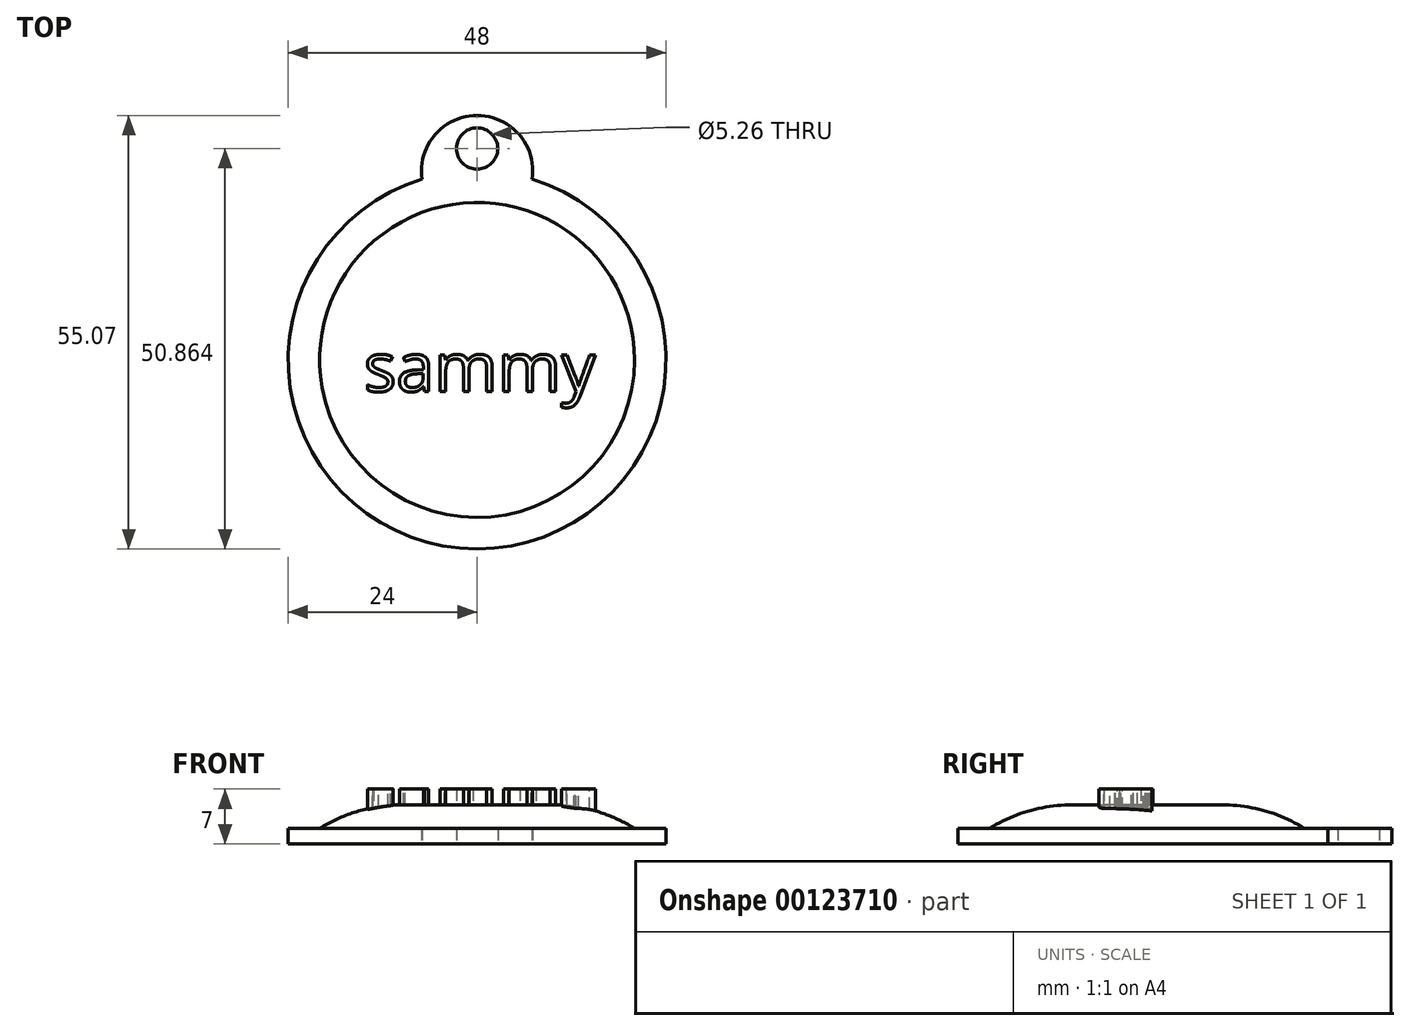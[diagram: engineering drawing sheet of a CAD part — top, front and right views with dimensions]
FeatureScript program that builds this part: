
annotation { "Feature Type Name" : "Feature", "Feature Type Description" : "" }
export const myFeature = defineFeature(function(context is Context, id is Id, definition is map)
    precondition{}
    {
        {
            var Q0;
            Q0=qCreatedBy(makeId("Top.planeOp"),FACE);
            var sketch = newSketch(context, id + "F0", { "sketchPlane" : qUnion([Q0])});
            skCircle(sketch, "E0", {"center": v(0, 0) * mm, "radius": 20 * mm});
            skCircle(sketch, "E1.0", {"center": v(0, 0) * mm, "radius": 24 * mm});
            skSolve(sketch);
        }
        {
            var Q0;
            Q0=makeQuery(id+"F0.imprint","IMPRINT",FACE,{"disambiguationData":[TD([[makeQuery(id+"F0.imprint","IMPRINT",EDGE,{"derivedFrom":sQuery(id+"F0.wireOp",EDGE,"E0")}),1.0]])]});
            var sketch = newSketch(context, id + "F1", { "sketchPlane" : qUnion([Q0])});
            skCircle(sketch, "E2", {"center": v(0, 0) * mm, "radius": 20 * mm});
            skSolve(sketch);
        }
        {
            var Q0;
            Q0 = qSketchRegion(id + "F1", true);
            extrude(context, id + "F2", {"entities" : qUnion([Q0]), "depth" : 5 * mm});
        }
        {
            var Q0;
            Q0=makeQuery(id+"F2.opExtrude","CAP_FACE",FACE,{"disambiguationData":[OSD([sQuery(id+"F1.wireOp",EDGE,"E2")])],"isStart":false});
            var sketch = newSketch(context, id + "F3", { "sketchPlane" : qUnion([Q0])});
            skText(sketch, "E3", { "text": "sammy", "fontName": "OpenSans-Regular.ttf"});
            const initialGuessF3  = {"E3": [-0.01439, -0.004, 1, 0, 0.00624]};
            skSetInitialGuess(sketch, initialGuessF3);
            skSolve(sketch);
        }
        {
            var Q0;
            Q0 = qSketchRegion(id + "F3", true);
            extrude(context, id + "F4", {"entities" : qUnion([Q0]), "operationType" : NewBodyOperationType.ADD, "endBound" : BoundingType.SYMMETRIC, "oppositeDirection" : true, "depth" : 4 * mm});
        }
        {
            var Q0;
            Q0=makeQuery(id+"F0.imprint","IMPRINT",FACE,{"disambiguationData":[TD([[makeQuery(id+"F0.imprint","IMPRINT",EDGE,{"derivedFrom":sQuery(id+"F0.wireOp",EDGE,"E0")}),-1.0]])]});
            extrude(context, id + "F5", {"entities" : qUnion([Q0]), "operationType" : NewBodyOperationType.ADD, "depth" : 2 * mm});
        }
        {
            var Q0;
            Q0=makeQuery(id+"F5.opExtrude","CAP_FACE",FACE,{"disambiguationData":[OSD([sQuery(id+"F0.wireOp",EDGE,"E0"),sQuery(id+"F0.wireOp",EDGE,"E1.0")])],"isStart":true});
            var sketch = newSketch(context, id + "F6", { "sketchPlane" : qUnion([Q0])});
            skCircle(sketch, "E4.0", {"center": v(0, 0) * mm, "radius": 20 * mm});
            skCircle(sketch, "E4.1", {"center": v(0, 0) * mm, "radius": 24 * mm});
            skArc(sketch, "E5", {"start": v(-7, -22.96) * mm, "mid": v(0, -31.07) * mm, "end": v(7, -22.96) * mm});
            skSolve(sketch);
        }
        {
            var Q0;
            {var subQ0=sQuery(id+"F6.wireOp",EDGE,"E5");Q0=makeQuery(id+"F6.imprint","IMPRINT",FACE,{"disambiguationData":[TD([[makeQuery(id+"F6.imprint","IMPRINT",EDGE,{"derivedFrom":subQ0}),1.0]])]});}
            extrude(context, id + "F7", {"entities" : qUnion([Q0]), "operationType" : NewBodyOperationType.ADD, "oppositeDirection" : true, "depth" : 2 * mm});
        }
        {
            var Q0;
            Q0=makeQuery(id+"F7.opExtrude","CAP_FACE",FACE,{"disambiguationData":[OSD([sQuery(id+"F6.wireOp",EDGE,"E4.1"),sQuery(id+"F6.wireOp",EDGE,"E5")])],"isStart":true});
            var sketch = newSketch(context, id + "F8", { "sketchPlane" : qUnion([Q0])});
            skCircle(sketch, "E6", {"center": v(0, -26.86) * mm, "radius": 2.63 * mm});
            skSolve(sketch);
        }
        {
            var Q0;
            Q0=makeQuery(id+"F8.imprint","IMPRINT",FACE,{"disambiguationData":[TD([[makeQuery(id+"F8.imprint","IMPRINT",EDGE,{"derivedFrom":sQuery(id+"F8.wireOp",EDGE,"E6")}),1.0]])]});
            extrude(context, id + "F9", {"entities" : qUnion([Q0]), "operationType" : NewBodyOperationType.REMOVE, "oppositeDirection" : true, "depth" : 2 * mm});
        }
        {
            var Q0;
            Q0=makeQuery(id+"F2.opExtrude","CAP_EDGE",EDGE,{"disambiguationData":[OSD([sQuery(id+"F1.wireOp",EDGE,"E2")])],"isStart":false});
            fillet(context, id + "F10", {"entities" : qUnion([Q0]), "radius" : 20 * mm, "tangentPropagation" : true, "allowEdgeOverflow" : false});
        }
    });
